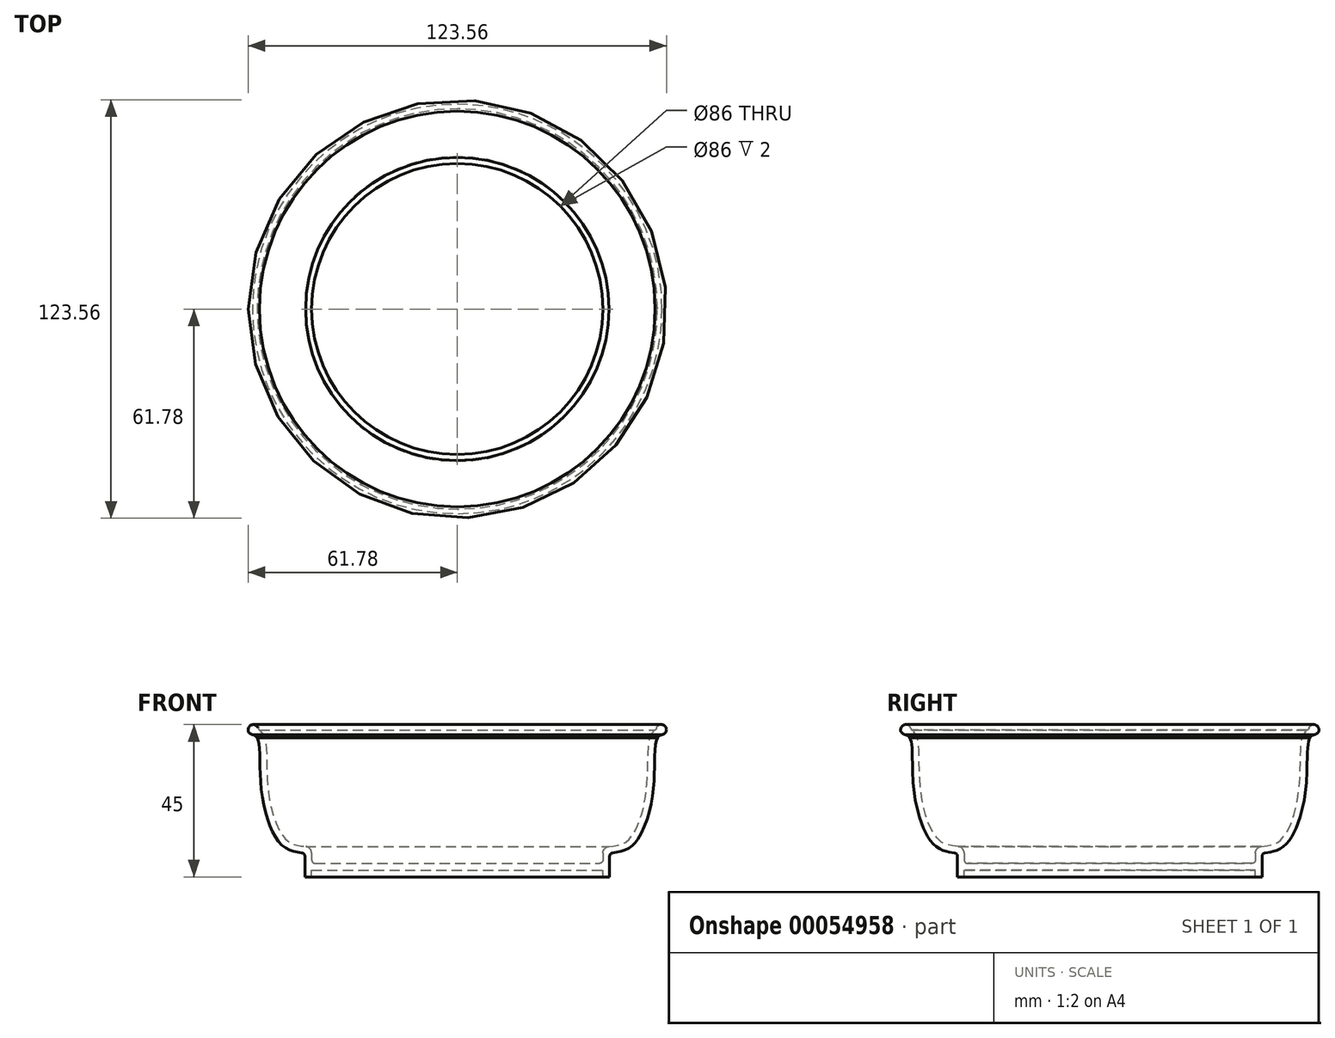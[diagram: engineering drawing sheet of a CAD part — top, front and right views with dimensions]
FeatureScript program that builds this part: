
annotation { "Feature Type Name" : "Feature", "Feature Type Description" : "" }
export const myFeature = defineFeature(function(context is Context, id is Id, definition is map)
    precondition{}
    {
        {
            var Q0;
            Q0=qCreatedBy(makeId("Front.planeOp"),FACE);
            var sketch = newSketch(context, id + "F0", { "sketchPlane" : qUnion([Q0])});
            skLineSegment(sketch, "E0", {"start": v(0, 0) * mm, "end": v(45, 0) * mm});
            skLineSegment(sketch, "E1", {"start": v(45, 0) * mm, "end": v(45, 4.1) * mm});
            skPoint(sketch, "E2", {"position": v(51.76, 7.36) * mm});
            skPoint(sketch, "E3", {"position": v(57.83, 23.5) * mm});
            skPoint(sketch, "E4", {"position": v(58.8, 38.41) * mm});
            skFitSpline(sketch, "E5", {"points": [v(60, 40) * mm, v(58.8, 38.41) * mm, v(57.83, 23.5) * mm, v(51.76, 7.36) * mm, v(45, 5) * mm], "startDerivative": vector(-11.79, -9.17) * mm, "endDerivative": vector(-32.3, -3.58) * mm});
            skLineSegment(sketch, "E6", {"start": v(0, 0) * mm, "end": v(0, 41.8) * mm, "construction": true});
            skLineSegment(sketch, "E7.0", {"start": v(43, 2) * mm, "end": v(43, 5) * mm});
            skLineSegment(sketch, "E7.1", {"start": v(0, 2) * mm, "end": v(43, 2) * mm});
            skArc(sketch, "E8", {"start": v(43, 5) * mm, "mid": v(43.5, 6.33) * mm, "end": v(44.78, 6.99) * mm});
            skFitSpline(sketch, "E9.0", {"points": [v(58.77, 41.58) * mm, v(58.65, 41.48) * mm, v(58.33, 41.24) * mm, v(57.83, 40.75) * mm, v(57.45, 40.22) * mm, v(57.19, 39.77) * mm, v(56.97, 39.28) * mm, v(56.8, 38.74) * mm, v(56.68, 38.2) * mm, v(56.55, 37.46) * mm, v(56.45, 36.47) * mm, v(56.37, 35.16) * mm, v(56.3, 33.25) * mm, v(56.26, 30.61) * mm, v(56.17, 27.74) * mm, v(56.02, 25.4) * mm, v(55.85, 23.64) * mm, v(55.6, 21.89) * mm, v(55.2, 19.59) * mm, v(54.54, 16.8) * mm, v(53.52, 13.79) * mm, v(52.52, 11.66) * mm, v(51.66, 10.28) * mm, v(51.12, 9.57) * mm, v(50.68, 9.09) * mm, v(50.36, 8.78) * mm, v(50.05, 8.52) * mm, v(49.62, 8.21) * mm, v(49.06, 7.9) * mm, v(48.1, 7.52) * mm, v(46.73, 7.2) * mm, v(45.45, 7.06) * mm, v(44.78, 6.99) * mm]});
            skArc(sketch, "E10.filletArc", {"start": v(45.88, 5.1) * mm, "mid": v(45.25, 4.77) * mm, "end": v(45, 4.1) * mm});
            skArc(sketch, "E11", {"start": v(60.48, 40.01) * mm, "mid": v(61.44, 42.44) * mm, "end": v(58.87, 42.02) * mm});
            skArc(sketch, "E12.filletArc", {"start": v(60.48, 40.01) * mm, "mid": v(59.7, 39.7) * mm, "end": v(59.12, 39.1) * mm});
            skArc(sketch, "E13.filletArc", {"start": v(58.32, 41.2) * mm, "mid": v(58.64, 41.58) * mm, "end": v(58.87, 42.02) * mm});
            skLineSegment(sketch, "E14", {"start": v(0, 0) * mm, "end": v(0, 2) * mm});
            skSolve(sketch);
        }
        {
            var Q0;
            Q0=qSketchRegion(id+"F0",true);
            var Q1;
            Q1=sQuery(id+"F0.wireOp",EDGE,"E5");
            var Q2;
            Q2=sQuery(id+"F0.wireOp",EDGE,"E1");
            var Q3;
            Q3=sQuery(id+"F0.wireOp",EDGE,"E0");
            var Q4;
            Q4=sQuery(id+"F0.wireOp",EDGE,"E7.1");
            var Q5;
            Q5=sQuery(id+"F0.wireOp",EDGE,"E7.0");
            var Q6;
            Q6=sQuery(id+"F0.wireOp",EDGE,"E8");
            var Q7;
            Q7=sQuery(id+"F0.wireOp",EDGE,"E9.0");
            var Q8;
            Q8=sQuery(id+"F0.wireOp",EDGE,"E6");
            revolve(context, id + "F1", {"entities" : qUnion([Q0]), "surfaceEntities" : qUnion([Q1, Q2, Q3, Q4, Q5, Q6, Q7]), "axis" : qUnion([Q8]), "revolveType" : RevolveType.FULL});
        }
        {
            var Q0;
            Q0=makeQuery(id+"F1.opRevolve","SWEPT_EDGE",EDGE,{"disambiguationData":[OSD([sQuery(id+"F0.wireOp",EDGE,"E7.0"),sQuery(id+"F0.wireOp",EDGE,"E7.1")])]});
            fillet(context, id + "F2", {"entities" : qUnion([Q0]), "radius" : 1 * mm, "tangentPropagation" : true, "allowEdgeOverflow" : false});
        }
        {
            var Q0;
            Q0=makeQuery(id+"F1.opRevolve","SWEPT_FACE",FACE,{"disambiguationData":[OSD([sQuery(id+"F0.wireOp",EDGE,"E0")])]});
            var sketch = newSketch(context, id + "F3", { "sketchPlane" : qUnion([Q0])});
            skCircle(sketch, "E15", {"center": v(0, 0) * mm, "radius": 43 * mm});
            skCircle(sketch, "E16", {"center": v(0, 0) * mm, "radius": 45 * mm});
            skSolve(sketch);
        }
        {
            var Q0;
            Q0=makeQuery(id+"F3.imprint","IMPRINT",FACE,{"disambiguationData":[TD([[makeQuery(id+"F3.imprint","IMPRINT",EDGE,{"derivedFrom":sQuery(id+"F3.wireOp",EDGE,"E15")}),-1.0]])]});
            var Q1;
            Q1=sQuery(id+"F3.wireOp",EDGE,"E15");
            var Q2;
            Q2=sQuery(id+"F3.wireOp",EDGE,"E16");
            extrude(context, id + "F4", {"entities" : qUnion([Q0]), "operationType" : NewBodyOperationType.ADD, "surfaceEntities" : qUnion([Q1, Q2]), "depth" : 2 * mm});
        }
    });
